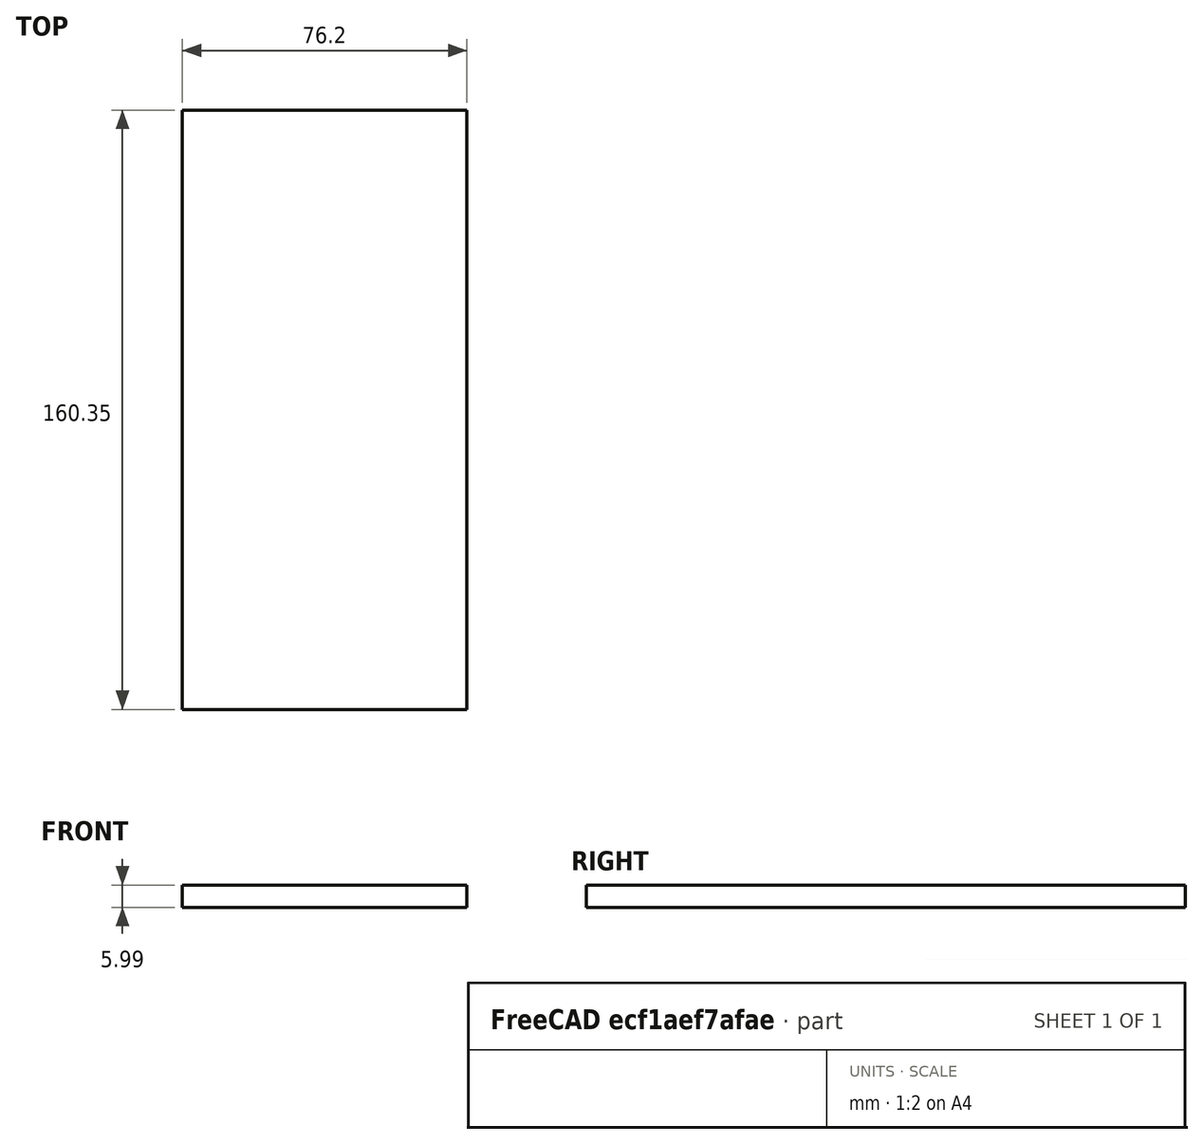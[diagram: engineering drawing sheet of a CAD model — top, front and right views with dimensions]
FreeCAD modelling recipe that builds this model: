
FCSTD DOCUMENT  (FreeCAD 0.19R24267 (Git))
Label: Inv2-P1
License: All rights reserved
LicenseURL: http://en.wikipedia.org/wiki/All_rights_reserved
objects: TechDraw::DrawViewDimension×3, TechDraw::DrawProjGroupItem×2, TechDraw::DrawHatch×2, TechDraw::DrawViewAnnotation×2, Sketcher::SketchObject×1, Part::Extrusion×1, TechDraw::DrawSVGTemplate×1, TechDraw::DrawProjGroup×1, TechDraw::DrawPage×1
note: 2 computed .brp shape members not serialized (recipe doc carries the construction recipe); baked Part::Feature solids carry a one-line shape summary decoded from their .brp

FEATURE [Sketcher::SketchObject] Sketch
  FullyConstrained = true
  sketch-geometry (4):
    g0: LineSegment StartX=0 StartY=0 StartZ=0 EndX=76.2 EndY=0 EndZ=0
    g1: LineSegment StartX=76.2 StartY=0 StartZ=0 EndX=76.2 EndY=-160.35 EndZ=0
    g2: LineSegment StartX=76.2 StartY=-160.35 StartZ=0 EndX=0 EndY=-160.35 EndZ=0
    g3: LineSegment StartX=0 StartY=-160.35 StartZ=0 EndX=0 EndY=0 EndZ=0
  constraints (11):
    c: Coincident(g0,g1)
    c: Coincident(g1,g2)
    c: Coincident(g2,g3)
    c: Coincident(g3,g0)
    c: Horizontal(g0)
    c: Horizontal(g2)
    c: Vertical(g1)
    c: Vertical(g3)
    c: Coincident(g0,g-1)
    c: DistanceX(g0,g0) = 76.2
    c: DistanceY(g3,g3) = 160.35
FEATURE [Part::Extrusion] Extrude
  Base = -> Sketch
  Dir = (0,0,1)
  DirMode = 2
  FaceMakerClass = Part::FaceMakerBullseye
  LengthFwd = 5.9944
  LengthRev = 0
  Solid = true
  Symmetric = false
FEATURE [TechDraw::DrawSVGTemplate] Template
  Height = 215.9
  Orientation = 1
  Width = 279.4
FEATURE [TechDraw::DrawProjGroupItem] ProjItem  label="Front"
  CoarseView = false
  Direction = (0,0,1)
  Focus = 100
  HardHidden = false
  IsoCount = 0
  IsoHidden = false
  IsoVisible = false
  LockPosition = true
  Perspective = false
  Rotation = 0
  RotationVector = (1,0,0)
  Scale = 0.5
  ScaleType = 2
  SeamHidden = false
  SeamVisible = true
  SmoothHidden = false
  SmoothVisible = true
  Source = -> [Extrude]
  Type = 0
  X = 0
  XDirection = (1,0,0)
  Y = 0
FEATURE [TechDraw::DrawProjGroupItem] ProjItem001  label="Left"
  CoarseView = false
  Direction = (-1,0,1e-16)
  Focus = 100
  HardHidden = false
  IsoCount = 0
  IsoHidden = false
  IsoVisible = false
  LockPosition = false
  Perspective = false
  Rotation = 0
  RotationVector = (1,0,0)
  Scale = 0.5
  ScaleType = 2
  SeamHidden = false
  SeamVisible = true
  SmoothHidden = false
  SmoothVisible = true
  Source = -> [Extrude]
  Type = 1
  X = 53.0372
  XDirection = (1e-16,0,1)
  Y = 0
FEATURE [TechDraw::DrawProjGroup] ProjGroup
  Anchor = -> ProjItem
  AutoDistribute = true
  LockPosition = false
  ProjectionType = 0
  Rotation = 0
  Scale = 0.5
  ScaleType = 2
  Source = -> [Extrude]
  Views = -> [ProjItem,ProjItem001]
  X = 123.342
  Y = 107.508
  spacingX = 15.0114
  spacingY = 15.0114
FEATURE [TechDraw::DrawHatch] Hatch  label="HatchF0"
  HatchPattern = <path>
  Source = -> ProjItem [Face0]
FEATURE [TechDraw::DrawHatch] Hatch001  label="Hatch001F0"
  HatchPattern = <path>
  Source = -> ProjItem001 [Face0]
FEATURE [TechDraw::DrawViewDimension] Dimension
  Arbitrary = false
  ArbitraryTolerances = false
  EqualTolerance = true
  FormatSpec = %.3f
  FormatSpecOverTolerance = %+.3f
  FormatSpecUnderTolerance = %+.3f
  Inverted = false
  LockPosition = false
  MeasureType = 1
  OverTolerance = 0
  References2D = -> [ProjItem]
  Rotation = 0
  ScaleType = 0
  TheoreticalExact = false
  Type = 2
  UnderTolerance = 0
  X = 28.6292
  Y = 1.10529
FEATURE [TechDraw::DrawViewDimension] Dimension001
  Arbitrary = false
  ArbitraryTolerances = false
  EqualTolerance = true
  FormatSpec = %.3f
  FormatSpecOverTolerance = %+.3f
  FormatSpecUnderTolerance = %+.3f
  Inverted = false
  LockPosition = false
  MeasureType = 1
  OverTolerance = 0
  References2D = -> [ProjItem]
  Rotation = 0
  ScaleType = 0
  TheoreticalExact = false
  Type = 1
  UnderTolerance = 0
  X = 0.36843
  Y = -45.9824
FEATURE [TechDraw::DrawViewDimension] Dimension002
  Arbitrary = false
  ArbitraryTolerances = false
  EqualTolerance = true
  FormatSpec = %.3f
  FormatSpecOverTolerance = %+.3f
  FormatSpecUnderTolerance = %+.3f
  Inverted = false
  LockPosition = false
  MeasureType = 1
  OverTolerance = 0
  References2D = -> [ProjItem001]
  Rotation = 0
  ScaleType = 0
  TheoreticalExact = false
  Type = 1
  UnderTolerance = 0
  X = 23.631
  Y = 26.5841
FEATURE [TechDraw::DrawViewAnnotation] Annotation
  Font = osifont
  LineSpace = 80
  LockPosition = false
  MaxWidth = -1
  Rotation = 0
  ScaleType = 0
  Text = Figure S2 (Inverted 2) | Panel 1 [front lower left] | Quantity: 1
  TextSize = 5.0038
  TextStyle = 0
  X = 36.7123
  Y = 195.58
FEATURE [TechDraw::DrawViewAnnotation] Annotation002
  Font = osifont
  LineSpace = 80
  LockPosition = false
  MaxWidth = -1
  Rotation = 0
  ScaleType = 0
  Text = Units: Inches
  TextSize = 5.0038
  TextStyle = 0
  X = 259.08
  Y = 5.08
FEATURE [TechDraw::DrawPage] Page
  KeepUpdated = true
  NextBalloonIndex = 1
  ProjectionType = 0
  Template = -> Template
  Views = -> [ProjGroup,Dimension,Dimension001,Dimension002,Annotation,Annotation002]
note: 2 file-system paths scrubbed to <path> (originals preserved in the JSON sidecar)
